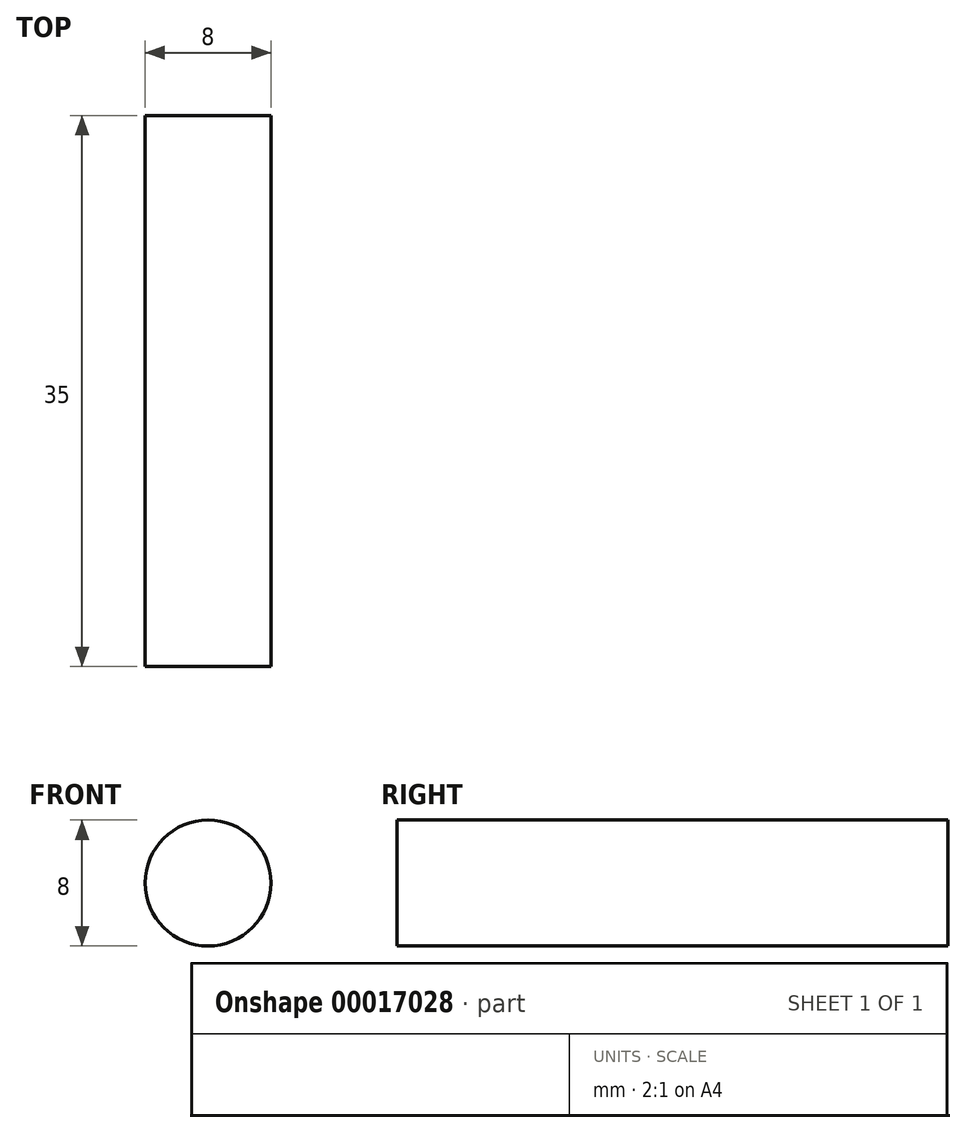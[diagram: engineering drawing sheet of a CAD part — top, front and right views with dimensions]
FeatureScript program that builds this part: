
annotation { "Feature Type Name" : "Feature", "Feature Type Description" : "" }
export const myFeature = defineFeature(function(context is Context, id is Id, definition is map)
    precondition{}
    {
        {
            var Q0;
            Q0=qCreatedBy(makeId("Front.planeOp"),FACE);
            var sketch = newSketch(context, id + "F0", { "sketchPlane" : qUnion([Q0])});
            skCircle(sketch, "E0", {"center": v(0, 0) * mm, "radius": 4 * mm});
            skSolve(sketch);
        }
        {
            var Q0;
            Q0 = qSketchRegion(id + "F0", true);
            extrude(context, id + "F1", {"entities" : qUnion([Q0]), "depth" : 35 * mm});
        }
    });
